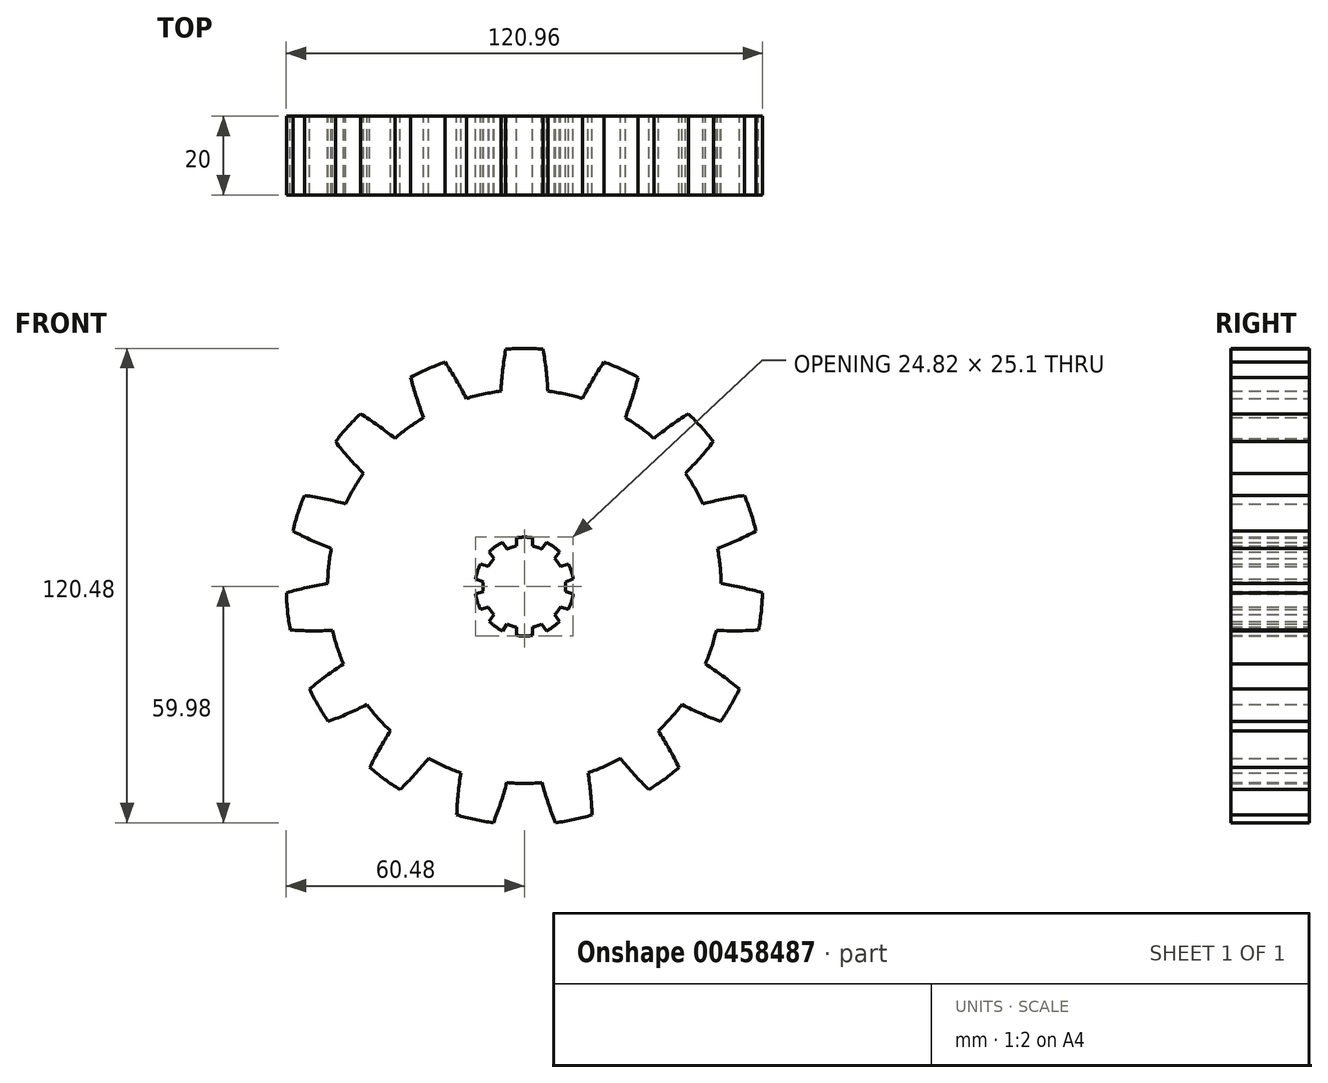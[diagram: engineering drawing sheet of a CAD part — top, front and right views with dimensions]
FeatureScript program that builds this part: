
annotation { "Feature Type Name" : "Feature", "Feature Type Description" : "" }
export const myFeature = defineFeature(function(context is Context, id is Id, definition is map)
    precondition{}
    {
        {
            var Q0;
            Q0=qCreatedBy(makeId("Front.planeOp"),FACE);
            var sketch = newSketch(context, id + "F0", { "sketchPlane" : qUnion([Q0])});
            skCircle(sketch, "E0", {"center": v(0, 0) * mm, "radius": 50 * mm});
            skCircle(sketch, "E1", {"center": v(0, 0) * mm, "radius": 10.5 * mm});
            skLineSegment(sketch, "E2", {"start": v(0, 50) * mm, "end": v(0, 46.5) * mm, "construction": true});
            skLineSegment(sketch, "E3", {"start": v(0, 46.5) * mm, "end": v(83.9, 46.5) * mm, "construction": true});
            skArc(sketch, "E4", {"start": v(-4.75, 60.31) * mm, "mid": v(-5.52, 55) * mm, "end": v(-5.97, 49.64) * mm});
            skArc(sketch, "E5.MirrorC", {"start": v(4.75, 60.31) * mm, "mid": v(5.52, 55) * mm, "end": v(5.97, 49.64) * mm});
            skArc(sketch, "E6.trimOffspring", {"start": v(4.75, 60.31) * mm, "mid": v(0, 60.5) * mm, "end": v(-4.75, 60.31) * mm});
            skArc(sketch, "E7.1.0", {"start": v(-20.2, 57.03) * mm, "mid": v(-24.6, 55.27) * mm, "end": v(-28.87, 53.17) * mm});
            skArc(sketch, "E7.1.1", {"start": v(-28.87, 53.17) * mm, "mid": v(-27.41, 48) * mm, "end": v(-25.64, 42.92) * mm});
            skArc(sketch, "E7.1.2", {"start": v(-20.2, 57.03) * mm, "mid": v(-17.33, 52.49) * mm, "end": v(-14.74, 47.78) * mm});
            skArc(sketch, "E7.2.0", {"start": v(-41.64, 43.89) * mm, "mid": v(-44.96, 40.48) * mm, "end": v(-48, 36.83) * mm});
            skArc(sketch, "E7.2.1", {"start": v(-48, 36.83) * mm, "mid": v(-44.56, 32.7) * mm, "end": v(-40.89, 28.78) * mm});
            skArc(sketch, "E7.2.2", {"start": v(-41.64, 43.89) * mm, "mid": v(-37.18, 40.9) * mm, "end": v(-32.9, 37.65) * mm});
            skArc(sketch, "E7.3.0", {"start": v(-55.9, 23.16) * mm, "mid": v(-57.54, 18.7) * mm, "end": v(-58.83, 14.12) * mm});
            skArc(sketch, "E7.3.1", {"start": v(-58.83, 14.12) * mm, "mid": v(-54, 11.75) * mm, "end": v(-49.06, 9.66) * mm});
            skArc(sketch, "E7.3.2", {"start": v(-55.9, 23.16) * mm, "mid": v(-50.6, 22.24) * mm, "end": v(-45.37, 21.02) * mm});
            skArc(sketch, "E7.4.0", {"start": v(-60.48, -1.58) * mm, "mid": v(-60.17, -6.32) * mm, "end": v(-59.49, -11.03) * mm});
            skArc(sketch, "E7.4.1", {"start": v(-59.49, -11.03) * mm, "mid": v(-54.12, -11.24) * mm, "end": v(-48.75, -11.13) * mm});
            skArc(sketch, "E7.4.2", {"start": v(-60.48, -1.58) * mm, "mid": v(-55.27, -0.26) * mm, "end": v(-50, 0.75) * mm});
            skArc(sketch, "E7.5.0", {"start": v(-54.6, -26.04) * mm, "mid": v(-52.4, -30.25) * mm, "end": v(-49.86, -34.27) * mm});
            skArc(sketch, "E7.5.1", {"start": v(-49.86, -34.27) * mm, "mid": v(-44.87, -32.28) * mm, "end": v(-40, -30) * mm});
            skArc(sketch, "E7.5.2", {"start": v(-54.6, -26.04) * mm, "mid": v(-50.39, -22.72) * mm, "end": v(-45.98, -19.65) * mm});
            skArc(sketch, "E7.6.0", {"start": v(-39.3, -46) * mm, "mid": v(-35.56, -48.95) * mm, "end": v(-31.6, -51.59) * mm});
            skArc(sketch, "E7.6.1", {"start": v(-31.6, -51.59) * mm, "mid": v(-27.86, -47.74) * mm, "end": v(-24.35, -43.67) * mm});
            skArc(sketch, "E7.6.2", {"start": v(-39.3, -46) * mm, "mid": v(-36.8, -41.25) * mm, "end": v(-34, -36.65) * mm});
            skArc(sketch, "E7.7.0", {"start": v(-17.19, -58) * mm, "mid": v(-12.58, -59.18) * mm, "end": v(-7.9, -59.98) * mm});
            skArc(sketch, "E7.7.1", {"start": v(-7.9, -59.98) * mm, "mid": v(-6.04, -54.94) * mm, "end": v(-4.48, -49.8) * mm});
            skArc(sketch, "E7.7.2", {"start": v(-17.19, -58) * mm, "mid": v(-16.83, -52.65) * mm, "end": v(-16.16, -47.32) * mm});
            skArc(sketch, "E7.8.0", {"start": v(7.9, -59.98) * mm, "mid": v(12.58, -59.18) * mm, "end": v(17.19, -58) * mm});
            skArc(sketch, "E7.8.1", {"start": v(17.19, -58) * mm, "mid": v(16.83, -52.65) * mm, "end": v(16.16, -47.32) * mm});
            skArc(sketch, "E7.8.2", {"start": v(7.9, -59.98) * mm, "mid": v(6.04, -54.94) * mm, "end": v(4.48, -49.8) * mm});
            skArc(sketch, "E7.9.0", {"start": v(31.6, -51.59) * mm, "mid": v(35.56, -48.95) * mm, "end": v(39.3, -46) * mm});
            skArc(sketch, "E7.9.1", {"start": v(39.3, -46) * mm, "mid": v(36.8, -41.25) * mm, "end": v(34, -36.65) * mm});
            skArc(sketch, "E7.9.2", {"start": v(31.6, -51.59) * mm, "mid": v(27.86, -47.74) * mm, "end": v(24.35, -43.67) * mm});
            skArc(sketch, "E7.10.0", {"start": v(49.86, -34.27) * mm, "mid": v(52.4, -30.25) * mm, "end": v(54.6, -26.04) * mm});
            skArc(sketch, "E7.10.1", {"start": v(54.6, -26.04) * mm, "mid": v(50.39, -22.72) * mm, "end": v(45.98, -19.65) * mm});
            skArc(sketch, "E7.10.2", {"start": v(49.86, -34.27) * mm, "mid": v(44.87, -32.28) * mm, "end": v(40, -30) * mm});
            skArc(sketch, "E7.11.0", {"start": v(59.49, -11.03) * mm, "mid": v(60.17, -6.32) * mm, "end": v(60.48, -1.58) * mm});
            skArc(sketch, "E7.11.1", {"start": v(60.48, -1.58) * mm, "mid": v(55.27, -0.26) * mm, "end": v(50, 0.75) * mm});
            skArc(sketch, "E7.11.2", {"start": v(59.49, -11.03) * mm, "mid": v(54.12, -11.24) * mm, "end": v(48.75, -11.13) * mm});
            skArc(sketch, "E7.12.0", {"start": v(58.83, 14.12) * mm, "mid": v(57.54, 18.7) * mm, "end": v(55.9, 23.16) * mm});
            skArc(sketch, "E7.12.1", {"start": v(55.9, 23.16) * mm, "mid": v(50.6, 22.24) * mm, "end": v(45.37, 21.02) * mm});
            skArc(sketch, "E7.12.2", {"start": v(58.83, 14.12) * mm, "mid": v(54, 11.75) * mm, "end": v(49.06, 9.66) * mm});
            skArc(sketch, "E7.13.0", {"start": v(48, 36.83) * mm, "mid": v(44.96, 40.48) * mm, "end": v(41.64, 43.89) * mm});
            skArc(sketch, "E7.13.1", {"start": v(41.64, 43.89) * mm, "mid": v(37.18, 40.9) * mm, "end": v(32.9, 37.65) * mm});
            skArc(sketch, "E7.13.2", {"start": v(48, 36.83) * mm, "mid": v(44.56, 32.7) * mm, "end": v(40.89, 28.78) * mm});
            skArc(sketch, "E7.14.0", {"start": v(28.87, 53.17) * mm, "mid": v(24.6, 55.27) * mm, "end": v(20.2, 57.03) * mm});
            skArc(sketch, "E7.14.1", {"start": v(20.2, 57.03) * mm, "mid": v(17.33, 52.49) * mm, "end": v(14.74, 47.78) * mm});
            skArc(sketch, "E7.14.2", {"start": v(28.87, 53.17) * mm, "mid": v(27.41, 48) * mm, "end": v(25.64, 42.92) * mm});
            skSolve(sketch);
        }
        {
            var Q0;
            Q0=makeQuery(id+"F0.imprint","IMPRINT",FACE,{"disambiguationData":[TD([[makeQuery(id+"F0.imprint","IMPRINT",EDGE,{"derivedFrom":sQuery(id+"F0.wireOp",EDGE,"E1")}),-1.0]])]});
            var Q1;
            Q1=makeQuery(id+"F0.imprint","IMPRINT",FACE,{"disambiguationData":[TD([[makeQuery(id+"F0.imprint","IMPRINT",EDGE,{"derivedFrom":sQuery(id+"F0.wireOp",EDGE,"E7.13.0")}),1.0]])]});
            var Q2;
            Q2=makeQuery(id+"F0.imprint","IMPRINT",FACE,{"disambiguationData":[TD([[makeQuery(id+"F0.imprint","IMPRINT",EDGE,{"derivedFrom":sQuery(id+"F0.wireOp",EDGE,"E7.12.0")}),1.0]])]});
            var Q3;
            Q3=makeQuery(id+"F0.imprint","IMPRINT",FACE,{"disambiguationData":[TD([[makeQuery(id+"F0.imprint","IMPRINT",EDGE,{"derivedFrom":sQuery(id+"F0.wireOp",EDGE,"E7.11.0")}),1.0]])]});
            var Q4;
            Q4=makeQuery(id+"F0.imprint","IMPRINT",FACE,{"disambiguationData":[TD([[makeQuery(id+"F0.imprint","IMPRINT",EDGE,{"derivedFrom":sQuery(id+"F0.wireOp",EDGE,"E7.10.0")}),1.0]])]});
            var Q5;
            Q5=makeQuery(id+"F0.imprint","IMPRINT",FACE,{"disambiguationData":[TD([[makeQuery(id+"F0.imprint","IMPRINT",EDGE,{"derivedFrom":sQuery(id+"F0.wireOp",EDGE,"E7.9.0")}),1.0]])]});
            var Q6;
            Q6=makeQuery(id+"F0.imprint","IMPRINT",FACE,{"disambiguationData":[TD([[makeQuery(id+"F0.imprint","IMPRINT",EDGE,{"derivedFrom":sQuery(id+"F0.wireOp",EDGE,"E7.8.0")}),1.0]])]});
            var Q7;
            Q7=makeQuery(id+"F0.imprint","IMPRINT",FACE,{"disambiguationData":[TD([[makeQuery(id+"F0.imprint","IMPRINT",EDGE,{"derivedFrom":sQuery(id+"F0.wireOp",EDGE,"E7.6.0")}),1.0]])]});
            var Q8;
            Q8=makeQuery(id+"F0.imprint","IMPRINT",FACE,{"disambiguationData":[TD([[makeQuery(id+"F0.imprint","IMPRINT",EDGE,{"derivedFrom":sQuery(id+"F0.wireOp",EDGE,"E7.7.0")}),1.0]])]});
            var Q9;
            Q9=makeQuery(id+"F0.imprint","IMPRINT",FACE,{"disambiguationData":[TD([[makeQuery(id+"F0.imprint","IMPRINT",EDGE,{"derivedFrom":sQuery(id+"F0.wireOp",EDGE,"E7.5.0")}),1.0]])]});
            var Q10;
            Q10=makeQuery(id+"F0.imprint","IMPRINT",FACE,{"disambiguationData":[TD([[makeQuery(id+"F0.imprint","IMPRINT",EDGE,{"derivedFrom":sQuery(id+"F0.wireOp",EDGE,"E7.4.0")}),1.0]])]});
            var Q11;
            Q11=makeQuery(id+"F0.imprint","IMPRINT",FACE,{"disambiguationData":[TD([[makeQuery(id+"F0.imprint","IMPRINT",EDGE,{"derivedFrom":sQuery(id+"F0.wireOp",EDGE,"E7.3.0")}),1.0]])]});
            var Q12;
            Q12=makeQuery(id+"F0.imprint","IMPRINT",FACE,{"disambiguationData":[TD([[makeQuery(id+"F0.imprint","IMPRINT",EDGE,{"derivedFrom":sQuery(id+"F0.wireOp",EDGE,"E7.2.0")}),1.0]])]});
            var Q13;
            Q13=makeQuery(id+"F0.imprint","IMPRINT",FACE,{"disambiguationData":[TD([[makeQuery(id+"F0.imprint","IMPRINT",EDGE,{"derivedFrom":sQuery(id+"F0.wireOp",EDGE,"E7.1.0")}),1.0]])]});
            var Q14;
            {var subQ0=sQuery(id+"F0.wireOp",EDGE,"E4");Q14=makeQuery(id+"F0.imprint","IMPRINT",FACE,{"disambiguationData":[TD([[makeQuery(id+"F0.imprint","IMPRINT",EDGE,{"derivedFrom":subQ0}),1.0]])]});}
            var Q15;
            Q15=makeQuery(id+"F0.imprint","IMPRINT",FACE,{"disambiguationData":[TD([[makeQuery(id+"F0.imprint","IMPRINT",EDGE,{"derivedFrom":sQuery(id+"F0.wireOp",EDGE,"E7.14.0")}),1.0]])]});
            extrude(context, id + "F1", {"entities" : qUnion([Q0, Q1, Q2, Q3, Q4, Q5, Q6, Q7, Q8, Q9, Q10, Q11, Q12, Q13, Q14, Q15]), "depth" : 20 * mm});
        }
        {
            var Q0;
            Q0=qCreatedBy(makeId("Front.planeOp"),FACE);
            var sketch = newSketch(context, id + "F2", { "sketchPlane" : qUnion([Q0])});
            skArc(sketch, "E8", {"start": v(2.05, 12.38) * mm, "mid": v(0, 12.55) * mm, "end": v(-2.05, 12.38) * mm});
            skLineSegment(sketch, "E9.left", {"start": v(2.05, 12.38) * mm, "end": v(2.05, -12.38) * mm});
            skLineSegment(sketch, "E9.right", {"start": v(-2.05, 12.38) * mm, "end": v(-2.05, -12.38) * mm});
            skPoint(sketch, "E10.orphan", {"position": v(-2.05, 12.55) * mm});
            skPoint(sketch, "E11.orphan", {"position": v(2.05, 12.55) * mm});
            skPoint(sketch, "E12.orphan", {"position": v(-2.05, -12.55) * mm});
            skPoint(sketch, "E13.orphan", {"position": v(2.05, -12.55) * mm});
            skArc(sketch, "E14.trimOffspring", {"start": v(-2.05, -12.38) * mm, "mid": v(0, -12.55) * mm, "end": v(2.05, -12.38) * mm});
            skArc(sketch, "E15.1.0", {"start": v(-5.62, 11.22) * mm, "mid": v(-7.38, 10.15) * mm, "end": v(-8.94, 8.81) * mm});
            skLineSegment(sketch, "E15.1.1", {"start": v(-5.62, 11.22) * mm, "end": v(8.94, -8.81) * mm});
            skArc(sketch, "E15.2.0", {"start": v(-11.14, 5.78) * mm, "mid": v(-11.94, 3.88) * mm, "end": v(-12.4, 1.88) * mm});
            skLineSegment(sketch, "E15.2.1", {"start": v(-11.14, 5.78) * mm, "end": v(12.4, -1.88) * mm});
            skArc(sketch, "E16.3.3.0", {"start": v(-12.4, -1.88) * mm, "mid": v(-11.94, -3.88) * mm, "end": v(-11.14, -5.78) * mm});
            skLineSegment(sketch, "E16.4.3.0", {"start": v(-12.4, -1.88) * mm, "end": v(11.14, 5.78) * mm});
            skArc(sketch, "E16.3.4.0", {"start": v(-8.94, -8.81) * mm, "mid": v(-7.38, -10.15) * mm, "end": v(-5.62, -11.22) * mm});
            skLineSegment(sketch, "E16.4.4.0", {"start": v(-8.94, -8.81) * mm, "end": v(5.62, 11.22) * mm});
            skLineSegment(sketch, "E16.4.5.0", {"start": v(-2.05, -12.38) * mm, "end": v(-2.05, 12.38) * mm});
            skArc(sketch, "E16.3.6.0", {"start": v(5.62, -11.22) * mm, "mid": v(7.38, -10.15) * mm, "end": v(8.94, -8.81) * mm});
            skLineSegment(sketch, "E16.4.6.0", {"start": v(5.62, -11.22) * mm, "end": v(-8.94, 8.81) * mm});
            skArc(sketch, "E16.3.7.0", {"start": v(11.14, -5.78) * mm, "mid": v(11.94, -3.88) * mm, "end": v(12.4, -1.88) * mm});
            skLineSegment(sketch, "E16.4.7.0", {"start": v(11.14, -5.78) * mm, "end": v(-12.4, 1.88) * mm});
            skArc(sketch, "E16.3.8.0", {"start": v(12.4, 1.88) * mm, "mid": v(11.94, 3.88) * mm, "end": v(11.14, 5.78) * mm});
            skLineSegment(sketch, "E16.4.8.0", {"start": v(12.4, 1.88) * mm, "end": v(-11.14, -5.78) * mm});
            skArc(sketch, "E16.3.9.0", {"start": v(8.94, 8.81) * mm, "mid": v(7.38, 10.15) * mm, "end": v(5.62, 11.22) * mm});
            skLineSegment(sketch, "E16.4.9.0", {"start": v(8.94, 8.81) * mm, "end": v(-5.62, -11.22) * mm});
            skCircle(sketch, "E17", {"center": v(0, 0) * mm, "radius": 10.5 * mm});
            skSolve(sketch);
        }
        {
            var Q0;
            Q0 = qSketchRegion(id + "F2", true);
            extrude(context, id + "F3", {"entities" : qUnion([Q0]), "operationType" : NewBodyOperationType.REMOVE, "depth" : 20 * mm});
        }
    });
